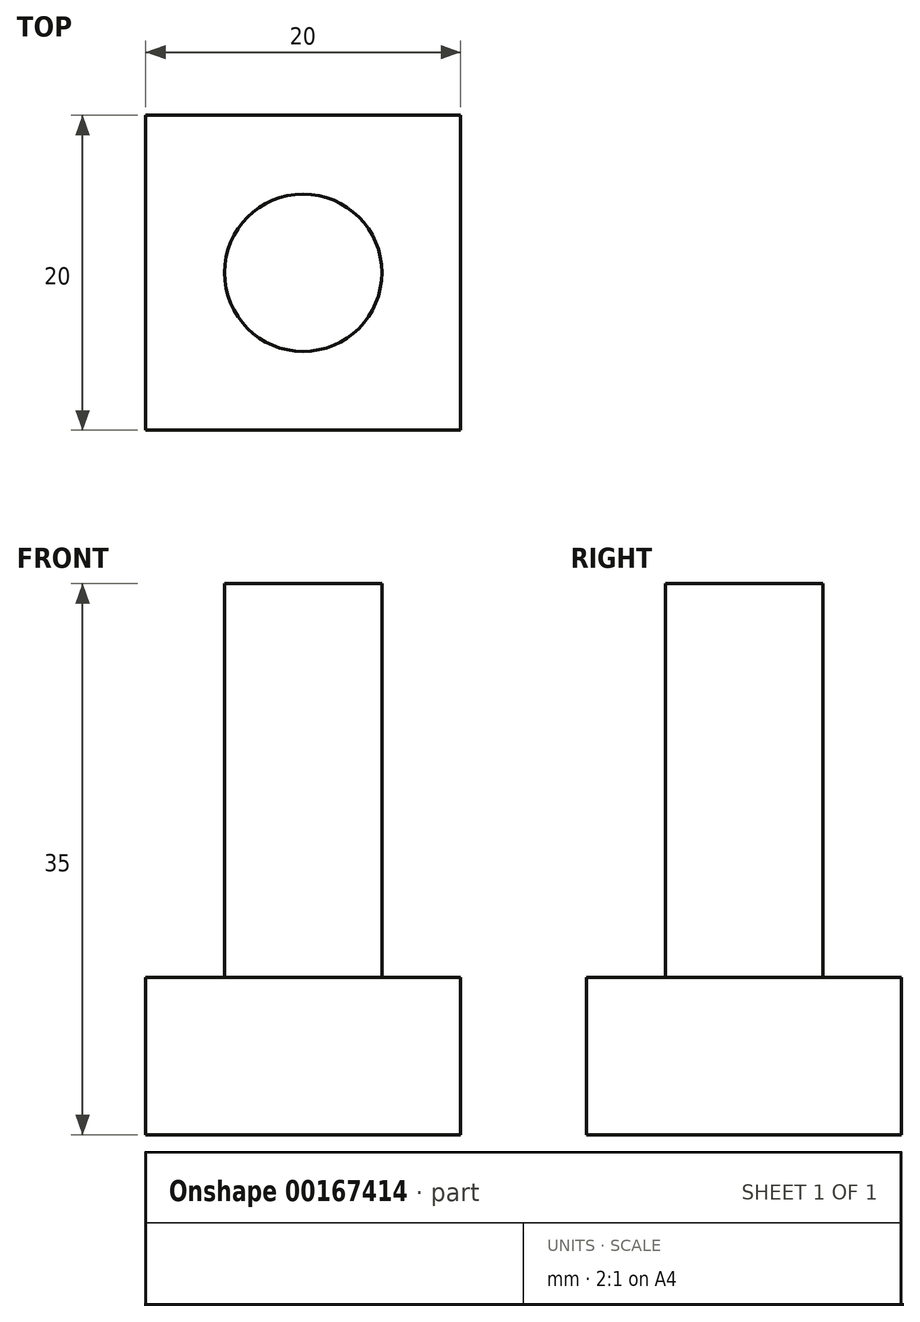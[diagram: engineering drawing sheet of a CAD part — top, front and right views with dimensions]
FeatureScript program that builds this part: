
annotation { "Feature Type Name" : "Feature", "Feature Type Description" : "" }
export const myFeature = defineFeature(function(context is Context, id is Id, definition is map)
    precondition{}
    {
        {
            var Q0;
            Q0=qCreatedBy(makeId("Top.planeOp"),FACE);
            var sketch = newSketch(context, id + "F0", { "sketchPlane" : qUnion([Q0])});
            skLineSegment(sketch, "E0.bottom", {"start": v(10, 10) * mm, "end": v(-10, 10) * mm});
            skLineSegment(sketch, "E0.top", {"start": v(10, -10) * mm, "end": v(-10, -10) * mm});
            skLineSegment(sketch, "E0.left", {"start": v(10, 10) * mm, "end": v(10, -10) * mm});
            skLineSegment(sketch, "E0.right", {"start": v(-10, 10) * mm, "end": v(-10, -10) * mm});
            skPoint(sketch, "E0.middle", {"position": v(0, 0) * mm});
            skSolve(sketch);
        }
        {
            var Q0;
            Q0=qSketchRegion(id+"F0",true);
            extrude(context, id + "F1", {"entities" : qUnion([Q0]), "depth" : 10 * mm});
        }
        {
            var Q0;
            Q0=makeQuery(id+"F1.opExtrude","CAP_FACE",FACE,{"disambiguationData":[OSD([sQuery(id+"F0.wireOp",EDGE,"E0.bottom"),sQuery(id+"F0.wireOp",EDGE,"E0.top"),sQuery(id+"F0.wireOp",EDGE,"E0.left"),sQuery(id+"F0.wireOp",EDGE,"E0.right")])],"isStart":false});
            var sketch = newSketch(context, id + "F2", { "sketchPlane" : qUnion([Q0])});
            skCircle(sketch, "E1", {"center": v(0, 0) * mm, "radius": 5 * mm});
            skSolve(sketch);
        }
        {
            var Q0;
            Q0=qSketchRegion(id+"F2",true);
            extrude(context, id + "F3", {"entities" : qUnion([Q0]), "operationType" : NewBodyOperationType.ADD, "depth" : 25 * mm});
        }
    });
